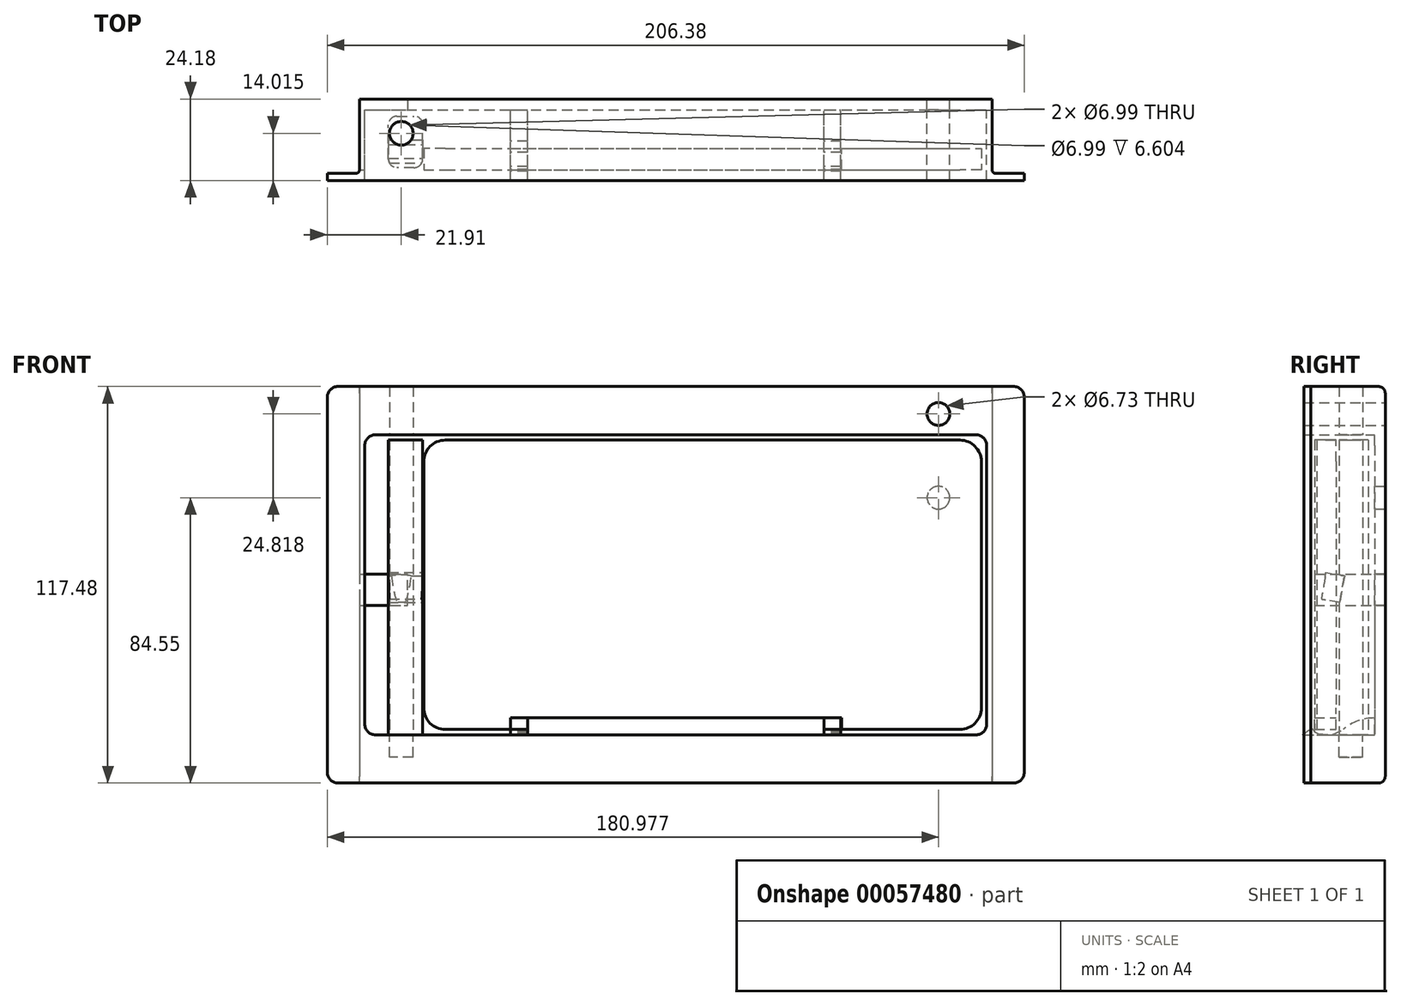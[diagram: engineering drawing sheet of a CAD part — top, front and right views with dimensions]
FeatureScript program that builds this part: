
annotation { "Feature Type Name" : "Feature", "Feature Type Description" : "" }
export const myFeature = defineFeature(function(context is Context, id is Id, definition is map)
    precondition{}
    {
        {
            var Q0;
            Q0=qCreatedBy(makeId("Front.planeOp"),FACE);
            var sketch = newSketch(context, id + "F0", { "sketchPlane" : qUnion([Q0])});
            skLineSegment(sketch, "E0.rect.bottom", {"start": v(-100.01, 58.74) * mm, "end": v(100.01, 58.74) * mm});
            skLineSegment(sketch, "E0.rect.top", {"start": v(-100.01, -58.74) * mm, "end": v(100.01, -58.74) * mm});
            skLineSegment(sketch, "E0.rect.left", {"start": v(-103.19, 55.56) * mm, "end": v(-103.19, -55.56) * mm});
            skLineSegment(sketch, "E0.rect.right", {"start": v(103.19, 55.56) * mm, "end": v(103.19, -55.56) * mm});
            skPoint(sketch, "E0.rect.middle", {"position": v(0, 0) * mm});
            skPoint(sketch, "E1.visualSharp", {"position": v(-103.19, 58.74) * mm});
            skArc(sketch, "E1.filletArc", {"start": v(-100.01, 58.74) * mm, "mid": v(-102.26, 57.8) * mm, "end": v(-103.19, 55.56) * mm});
            skPoint(sketch, "E2.visualSharp", {"position": v(103.19, 58.74) * mm});
            skArc(sketch, "E2.filletArc", {"start": v(103.19, 55.56) * mm, "mid": v(102.26, 57.8) * mm, "end": v(100.01, 58.74) * mm});
            skPoint(sketch, "E3.visualSharp", {"position": v(103.19, -58.74) * mm});
            skArc(sketch, "E3.filletArc", {"start": v(100.01, -58.74) * mm, "mid": v(102.26, -57.8) * mm, "end": v(103.19, -55.56) * mm});
            skPoint(sketch, "E4.visualSharp", {"position": v(-103.19, -58.74) * mm});
            skArc(sketch, "E4.filletArc", {"start": v(-103.19, -55.56) * mm, "mid": v(-102.26, -57.8) * mm, "end": v(-100.01, -58.74) * mm});
            skLineSegment(sketch, "E5.1", {"start": v(-92.07, 41.27) * mm, "end": v(-92.07, -41.28) * mm});
            skLineSegment(sketch, "E5.5", {"start": v(92.08, 41.28) * mm, "end": v(92.08, -41.27) * mm});
            skLineSegment(sketch, "E6", {"start": v(-88.9, 44.45) * mm, "end": v(88.9, 44.45) * mm});
            skLineSegment(sketch, "E7", {"start": v(-88.9, -44.45) * mm, "end": v(88.9, -44.45) * mm});
            skArc(sketch, "E8.filletArc", {"start": v(92.08, 41.28) * mm, "mid": v(91.15, 43.52) * mm, "end": v(88.9, 44.45) * mm});
            skArc(sketch, "E9.filletArc", {"start": v(88.9, -44.45) * mm, "mid": v(91.15, -43.52) * mm, "end": v(92.08, -41.27) * mm});
            skArc(sketch, "E10.filletArc", {"start": v(-92.07, -41.28) * mm, "mid": v(-91.15, -43.52) * mm, "end": v(-88.9, -44.45) * mm});
            skArc(sketch, "E11.filletArc", {"start": v(-88.9, 44.45) * mm, "mid": v(-91.15, 43.52) * mm, "end": v(-92.07, 41.27) * mm});
            skLineSegment(sketch, "E12", {"start": v(-103.19, 3.17) * mm, "end": v(-92.07, 3.17) * mm});
            skLineSegment(sketch, "E13", {"start": v(-103.19, -3.18) * mm, "end": v(-92.07, -3.18) * mm});
            skPoint(sketch, "E14.end.orphan", {"position": v(-103.19, 0) * mm});
            skPoint(sketch, "E14.start.orphan", {"position": v(-92.07, 0) * mm});
            skLineSegment(sketch, "E15", {"start": v(-92.07, 3.17) * mm, "end": v(-79.37, 3.17) * mm});
            skLineSegment(sketch, "E16", {"start": v(-92.07, -3.18) * mm, "end": v(-79.37, -3.18) * mm});
            skLineSegment(sketch, "E17", {"start": v(-79.37, -3.18) * mm, "end": v(-79.37, 3.17) * mm});
            skSolve(sketch);
        }
        {
            var Q0;
            Q0=makeQuery(id+"F0.imprint","IMPRINT",FACE,{"disambiguationData":[TD([[makeQuery(id+"F0.imprint","IMPRINT",EDGE,{"derivedFrom":sQuery(id+"F0.wireOp",EDGE,"E0.rect.bottom")}),-1.0]])]});
            var Q1;
            Q1=makeQuery(id+"F0.imprint","IMPRINT",FACE,{"disambiguationData":[TD([[makeQuery(id+"F0.imprint","IMPRINT",EDGE,{"derivedFrom":sQuery(id+"F0.wireOp",EDGE,"E5.5")}),-1.0]])]});
            extrude(context, id + "F1", {"entities" : qUnion([Q0, Q1]), "oppositeDirection" : true, "depth" : 3.17 * mm});
        }
        {
            var Q0;
            Q0=makeQuery(id+"F0.imprint","IMPRINT",FACE,{"disambiguationData":[TD([[makeQuery(id+"F0.imprint","IMPRINT",EDGE,{"derivedFrom":sQuery(id+"F0.wireOp",EDGE,"E0.rect.bottom")}),-1.0]])]});
            extrude(context, id + "F2", {"entities" : qUnion([Q0]), "operationType" : NewBodyOperationType.ADD, "depth" : 17.78 * mm});
        }
        {
            var Q0;
            Q0=makeQuery(id+"F2.opExtrude","CAP_FACE",FACE,{"disambiguationData":[OSD([sQuery(id+"F0.wireOp",EDGE,"E0.rect.bottom"),sQuery(id+"F0.wireOp",EDGE,"E0.rect.top"),sQuery(id+"F0.wireOp",EDGE,"E0.rect.left"),sQuery(id+"F0.wireOp",EDGE,"E0.rect.right"),sQuery(id+"F0.wireOp",EDGE,"E1.filletArc"),sQuery(id+"F0.wireOp",EDGE,"E2.filletArc"),sQuery(id+"F0.wireOp",EDGE,"E3.filletArc"),sQuery(id+"F0.wireOp",EDGE,"E4.filletArc"),sQuery(id+"F0.wireOp",EDGE,"E5.1"),sQuery(id+"F0.wireOp",EDGE,"E5.5"),sQuery(id+"F0.wireOp",EDGE,"E6"),sQuery(id+"F0.wireOp",EDGE,"E7"),sQuery(id+"F0.wireOp",EDGE,"E8.filletArc"),sQuery(id+"F0.wireOp",EDGE,"E9.filletArc"),sQuery(id+"F0.wireOp",EDGE,"E10.filletArc"),sQuery(id+"F0.wireOp",EDGE,"E11.filletArc"),sQuery(id+"F0.wireOp",EDGE,"E12"),sQuery(id+"F0.wireOp",EDGE,"E13")])],"isStart":false});
            var sketch = newSketch(context, id + "F3", { "sketchPlane" : qUnion([Q0])});
            skLineSegment(sketch, "E18", {"start": v(-88.9, 44.45) * mm, "end": v(88.9, 44.45) * mm});
            skLineSegment(sketch, "E19", {"start": v(92.08, 41.28) * mm, "end": v(92.08, -41.27) * mm});
            skLineSegment(sketch, "E20", {"start": v(88.9, -44.45) * mm, "end": v(-88.9, -44.45) * mm});
            skLineSegment(sketch, "E21", {"start": v(-92.07, -41.27) * mm, "end": v(-92.07, 41.27) * mm});
            skPoint(sketch, "E22.start.orphan", {"position": v(-91.15, 43.52) * mm});
            skLineSegment(sketch, "E23", {"start": v(-100.01, 58.74) * mm, "end": v(-100.01, 58.74) * mm});
            skLineSegment(sketch, "E24", {"start": v(-103.19, 55.56) * mm, "end": v(-103.19, -55.56) * mm});
            skLineSegment(sketch, "E25", {"start": v(-100.01, -58.74) * mm, "end": v(100.01, -58.74) * mm});
            skLineSegment(sketch, "E26", {"start": v(103.19, -55.56) * mm, "end": v(103.19, 55.56) * mm});
            skLineSegment(sketch, "E27", {"start": v(100.01, 58.74) * mm, "end": v(-100.01, 58.74) * mm});
            skPoint(sketch, "E28.visualSharp", {"position": v(-103.19, 58.74) * mm});
            skArc(sketch, "E28.filletArc", {"start": v(-100.01, 58.74) * mm, "mid": v(-102.26, 57.8) * mm, "end": v(-103.19, 55.56) * mm});
            skPoint(sketch, "E29.visualSharp", {"position": v(-92.07, 44.45) * mm});
            skArc(sketch, "E29.filletArc", {"start": v(-88.9, 44.45) * mm, "mid": v(-91.15, 43.52) * mm, "end": v(-92.07, 41.27) * mm});
            skPoint(sketch, "E30.visualSharp", {"position": v(92.08, 44.45) * mm});
            skArc(sketch, "E30.filletArc", {"start": v(92.08, 41.28) * mm, "mid": v(91.15, 43.52) * mm, "end": v(88.9, 44.45) * mm});
            skPoint(sketch, "E31.visualSharp", {"position": v(103.19, 58.74) * mm});
            skArc(sketch, "E31.filletArc", {"start": v(103.19, 55.56) * mm, "mid": v(102.26, 57.8) * mm, "end": v(100.01, 58.74) * mm});
            skPoint(sketch, "E32.visualSharp", {"position": v(92.08, -44.45) * mm});
            skArc(sketch, "E32.filletArc", {"start": v(88.9, -44.45) * mm, "mid": v(91.15, -43.52) * mm, "end": v(92.08, -41.27) * mm});
            skPoint(sketch, "E33.visualSharp", {"position": v(103.19, -58.74) * mm});
            skArc(sketch, "E33.filletArc", {"start": v(100.01, -58.74) * mm, "mid": v(102.26, -57.8) * mm, "end": v(103.19, -55.56) * mm});
            skPoint(sketch, "E34.visualSharp", {"position": v(-103.19, -58.74) * mm});
            skArc(sketch, "E34.filletArc", {"start": v(-103.19, -55.56) * mm, "mid": v(-102.26, -57.8) * mm, "end": v(-100.01, -58.74) * mm});
            skPoint(sketch, "E35.visualSharp", {"position": v(-92.07, -44.45) * mm});
            skArc(sketch, "E35.filletArc", {"start": v(-92.07, -41.27) * mm, "mid": v(-91.15, -43.52) * mm, "end": v(-88.9, -44.45) * mm});
            skSolve(sketch);
        }
        {
            var Q0;
            Q0=makeQuery(id+"F3.imprint","IMPRINT",FACE,{"disambiguationData":[TD([[makeQuery(id+"F3.imprint","IMPRINT",EDGE,{"derivedFrom":sQuery(id+"F3.wireOp",EDGE,"E18")}),1.0]])]});
            var Q1;
            {var subQ1=makeQuery(id+"F2.opExtrude","CAP_EDGE",EDGE,{"disambiguationData":[OSD([sQuery(id+"F0.wireOp",EDGE,"E12")])],"isStart":false});Q1=makeQuery(id+"F3.imprint","IMPRINT",FACE,{"disambiguationData":[TD([[makeQuery(id+"F3.imprint","IMPRINT",EDGE,{"derivedFrom":subQ1}),-1.0]])]});}
            extrude(context, id + "F4", {"entities" : qUnion([Q0, Q1]), "operationType" : NewBodyOperationType.ADD, "depth" : 3.17 * mm});
        }
        {
            var Q0;
            Q0=makeQuery(id+"F4.opExtrude","CAP_FACE",FACE,{"disambiguationData":[OSD([sQuery(id+"F3.wireOp",EDGE,"E18"),sQuery(id+"F3.wireOp",EDGE,"E19"),sQuery(id+"F3.wireOp",EDGE,"E20"),sQuery(id+"F3.wireOp",EDGE,"E21"),sQuery(id+"F3.wireOp",EDGE,"E24"),sQuery(id+"F3.wireOp",EDGE,"E25"),sQuery(id+"F3.wireOp",EDGE,"E26"),sQuery(id+"F3.wireOp",EDGE,"E27"),sQuery(id+"F3.wireOp",EDGE,"E28.filletArc"),sQuery(id+"F3.wireOp",EDGE,"E29.filletArc"),sQuery(id+"F3.wireOp",EDGE,"E30.filletArc"),sQuery(id+"F3.wireOp",EDGE,"E31.filletArc"),sQuery(id+"F3.wireOp",EDGE,"E32.filletArc"),sQuery(id+"F3.wireOp",EDGE,"E33.filletArc"),sQuery(id+"F3.wireOp",EDGE,"E34.filletArc"),sQuery(id+"F3.wireOp",EDGE,"E35.filletArc")])],"isStart":true});
            var sketch = newSketch(context, id + "F5", { "sketchPlane" : qUnion([Q0])});
            skLineSegment(sketch, "E36.rect.bottom", {"start": v(68.26, 42.86) * mm, "end": v(-84.14, 42.86) * mm});
            skLineSegment(sketch, "E36.rect.top", {"start": v(68.26, -42.86) * mm, "end": v(-84.14, -42.86) * mm});
            skLineSegment(sketch, "E36.rect.left", {"start": v(74.61, 36.51) * mm, "end": v(74.61, -36.51) * mm});
            skLineSegment(sketch, "E36.rect.right", {"start": v(-90.49, 36.51) * mm, "end": v(-90.49, -36.51) * mm});
            skPoint(sketch, "E36.rect.middle", {"position": v(-7.94, 0) * mm});
            skPoint(sketch, "E37.visualSharp", {"position": v(74.61, 42.86) * mm});
            skArc(sketch, "E37.filletArc", {"start": v(74.61, 36.51) * mm, "mid": v(72.75, 41) * mm, "end": v(68.26, 42.86) * mm});
            skPoint(sketch, "E38.visualSharp", {"position": v(-90.49, 42.86) * mm});
            skArc(sketch, "E38.filletArc", {"start": v(-84.14, 42.86) * mm, "mid": v(-88.63, 41) * mm, "end": v(-90.49, 36.51) * mm});
            skPoint(sketch, "E39.visualSharp", {"position": v(-90.49, -42.86) * mm});
            skArc(sketch, "E39.filletArc", {"start": v(-90.49, -36.51) * mm, "mid": v(-88.63, -41) * mm, "end": v(-84.14, -42.86) * mm});
            skPoint(sketch, "E40.visualSharp", {"position": v(74.61, -42.86) * mm});
            skArc(sketch, "E40.filletArc", {"start": v(68.26, -42.86) * mm, "mid": v(72.75, -41) * mm, "end": v(74.61, -36.51) * mm});
            skSolve(sketch);
        }
        {
            var Q0;
            Q0=makeQuery(id+"F5.imprint","IMPRINT",FACE,{"disambiguationData":[TD([[makeQuery(id+"F5.imprint","IMPRINT",EDGE,{"derivedFrom":sQuery(id+"F5.wireOp",EDGE,"E36.rect.bottom")}),1.0]])]});
            extrude(context, id + "F6", {"entities" : qUnion([Q0]), "operationType" : NewBodyOperationType.ADD, "depth" : 6.35 * mm});
        }
        {
            var Q0;
            Q0=makeQuery(id+"F4.boolean.opBoolean","MERGE",FACE,{"derivedFrom":[makeQuery(id+"F2.opExtrude","SWEPT_FACE",FACE,{"disambiguationData":[OSD([sQuery(id+"F0.wireOp",EDGE,"E6")])]}),makeQuery(id+"F4.opExtrude","SWEPT_FACE",FACE,{"disambiguationData":[OSD([sQuery(id+"F3.wireOp",EDGE,"E18")])]})]});
            var sketch = newSketch(context, id + "F7", { "sketchPlane" : qUnion([Q0])});
            skCircle(sketch, "E41", {"center": v(-81.28, 6.98) * mm, "radius": 3.5 * mm});
            skSolve(sketch);
        }
        {
            var Q0;
            Q0=makeQuery(id+"F7.imprint","IMPRINT",FACE,{"disambiguationData":[TD([[makeQuery(id+"F7.imprint","IMPRINT",EDGE,{"derivedFrom":sQuery(id+"F7.wireOp",EDGE,"E41")}),1.0]])]});
            extrude(context, id + "F8", {"entities" : qUnion([Q0]), "operationType" : NewBodyOperationType.REMOVE, "endBound" : BoundingType.UP_TO_NEXT, "oppositeDirection" : true, "depth" : 6.35 * mm});
        }
        {
            var Q0;
            Q0=makeQuery(id+"F4.boolean.opBoolean","MERGE",FACE,{"derivedFrom":[makeQuery(id+"F2.opExtrude","SWEPT_FACE",FACE,{"disambiguationData":[OSD([sQuery(id+"F0.wireOp",EDGE,"E7")])]}),makeQuery(id+"F4.opExtrude","SWEPT_FACE",FACE,{"disambiguationData":[OSD([sQuery(id+"F3.wireOp",EDGE,"E20")])]})]});
            var sketch = newSketch(context, id + "F9", { "sketchPlane" : qUnion([Q0])});
            skCircle(sketch, "E42", {"center": v(-81.28, -6.98) * mm, "radius": 3.5 * mm});
            skSolve(sketch);
        }
        {
            var Q0;
            Q0=makeQuery(id+"F9.imprint","IMPRINT",FACE,{"disambiguationData":[TD([[makeQuery(id+"F9.imprint","IMPRINT",EDGE,{"derivedFrom":sQuery(id+"F9.wireOp",EDGE,"E42")}),1.0]])]});
            extrude(context, id + "F10", {"entities" : qUnion([Q0]), "operationType" : NewBodyOperationType.REMOVE, "oppositeDirection" : true, "depth" : 6.6 * mm});
        }
        {
            var Q0;
            Q0=makeQuery(id+"F4.boolean.opBoolean","MERGE",FACE,{"derivedFrom":[makeQuery(id+"F2.opExtrude","SWEPT_FACE",FACE,{"disambiguationData":[OSD([sQuery(id+"F0.wireOp",EDGE,"E7")])]}),makeQuery(id+"F4.opExtrude","SWEPT_FACE",FACE,{"disambiguationData":[OSD([sQuery(id+"F3.wireOp",EDGE,"E20")])]})]});
            var sketch = newSketch(context, id + "F11", { "sketchPlane" : qUnion([Q0])});
            skCircle(sketch, "E43", {"center": v(-81.28, -6.98) * mm, "radius": 3.3 * mm});
            skLineSegment(sketch, "E44", {"start": v(-74.93, -17.14) * mm, "end": v(-85.1, -17.14) * mm});
            skLineSegment(sketch, "E45", {"start": v(-85.1, -17.14) * mm, "end": v(-85.1, -1.9) * mm});
            skLineSegment(sketch, "E46", {"start": v(-85.1, -1.9) * mm, "end": v(-74.93, -1.9) * mm});
            skLineSegment(sketch, "E47", {"start": v(-74.93, -17.14) * mm, "end": v(-74.93, -1.9) * mm});
            skSolve(sketch);
        }
        {
            var Q0;
            Q0=makeQuery(id+"F11.imprint","IMPRINT",FACE,{"disambiguationData":[TD([[makeQuery(id+"F11.imprint","IMPRINT",EDGE,{"derivedFrom":sQuery(id+"F11.wireOp",EDGE,"E44")}),-1.0]])]});
            var Q1;
            Q1 = qSketchRegion(id + "F13", true);
            extrude(context, id + "F12", {"entities" : qUnion([Q0, Q1]), "depth" : 87.31 * mm});
        }
        {
            var Q0;
            Q0=makeQuery(id+"F12.opExtrude","SWEPT_FACE",FACE,{"disambiguationData":[OSD([sQuery(id+"F11.wireOp",EDGE,"E47")])]});
            var sketch = newSketch(context, id + "F13", { "sketchPlane" : qUnion([Q0])});
            skPoint(sketch, "E48.rect.middle", {"position": v(-10.27, -5.18) * mm});
            skLineSegment(sketch, "E49", {"start": v(-10.27, -5.18) * mm, "end": v(-15.74, -4.21) * mm});
            skLineSegment(sketch, "E50", {"start": v(-15.74, -4.21) * mm, "end": v(-14.37, 3.6) * mm});
            skLineSegment(sketch, "E51", {"start": v(-14.37, 3.6) * mm, "end": v(-8.9, 2.64) * mm});
            skLineSegment(sketch, "E52", {"start": v(-8.9, 2.64) * mm, "end": v(-10.27, -5.18) * mm});
            skPoint(sketch, "E53.end.orphan", {"position": v(-15.05, -0.3) * mm});
            skPoint(sketch, "E53.start.orphan", {"position": v(-12.32, -0.79) * mm});
            skSolve(sketch);
        }
        {
            var Q0;
            Q0=makeQuery(id+"F13.imprint","IMPRINT",FACE,{"disambiguationData":[TD([[makeQuery(id+"F13.imprint","IMPRINT",EDGE,{"derivedFrom":sQuery(id+"F13.wireOp",EDGE,"E49")}),-1.0]])]});
            extrude(context, id + "F14", {"entities" : qUnion([Q0]), "operationType" : NewBodyOperationType.REMOVE, "endBound" : BoundingType.UP_TO_NEXT, "oppositeDirection" : true, "depth" : 25.4 * mm});
        }
        {
            var Q0;
            Q0=makeQuery(id+"F12.opExtrude","SWEPT_EDGE",EDGE,{"disambiguationData":[OSD([sQuery(id+"F11.wireOp",EDGE,"E44"),sQuery(id+"F11.wireOp",EDGE,"E45")])]});
            var Q1;
            Q1=makeQuery(id+"F12.opExtrude","SWEPT_EDGE",EDGE,{"disambiguationData":[OSD([sQuery(id+"F11.wireOp",EDGE,"E44"),sQuery(id+"F11.wireOp",EDGE,"E47")])]});
            var Q2;
            Q2=makeQuery(id+"F12.opExtrude","SWEPT_EDGE",EDGE,{"disambiguationData":[OSD([sQuery(id+"F11.wireOp",EDGE,"E46"),sQuery(id+"F11.wireOp",EDGE,"E47")])]});
            var Q3;
            Q3=makeQuery(id+"F12.opExtrude","SWEPT_EDGE",EDGE,{"disambiguationData":[OSD([sQuery(id+"F11.wireOp",EDGE,"E45"),sQuery(id+"F11.wireOp",EDGE,"E46")])]});
            fillet(context, id + "F15", {"entities" : qUnion([Q0, Q1, Q2, Q3]), "radius" : 2.54 * mm, "tangentPropagation" : true, "allowEdgeOverflow" : false});
        }
        {
            var Q0;
            Q0=makeQuery(id+"F1.opExtrude","CAP_FACE",FACE,{"disambiguationData":[OSD([sQuery(id+"F0.wireOp",EDGE,"E0.rect.bottom"),sQuery(id+"F0.wireOp",EDGE,"E0.rect.top"),sQuery(id+"F0.wireOp",EDGE,"E0.rect.left"),sQuery(id+"F0.wireOp",EDGE,"E0.rect.right"),sQuery(id+"F0.wireOp",EDGE,"E1.filletArc"),sQuery(id+"F0.wireOp",EDGE,"E2.filletArc"),sQuery(id+"F0.wireOp",EDGE,"E3.filletArc"),sQuery(id+"F0.wireOp",EDGE,"E4.filletArc"),sQuery(id+"F0.wireOp",EDGE,"E12"),sQuery(id+"F0.wireOp",EDGE,"E13"),sQuery(id+"F0.wireOp",EDGE,"E15"),sQuery(id+"F0.wireOp",EDGE,"E16"),sQuery(id+"F0.wireOp",EDGE,"E17")])],"isStart":false});
            var sketch = newSketch(context, id + "F16", { "sketchPlane" : qUnion([Q0])});
            skCircle(sketch, "E54", {"center": v(-77.79, 50.63) * mm, "radius": 3.37 * mm});
            skCircle(sketch, "E55", {"center": v(-77.79, 25.81) * mm, "radius": 3.37 * mm});
            skSolve(sketch);
        }
        {
            var Q0;
            Q0=makeQuery(id+"F16.imprint","IMPRINT",FACE,{"disambiguationData":[TD([[makeQuery(id+"F16.imprint","IMPRINT",EDGE,{"derivedFrom":sQuery(id+"F16.wireOp",EDGE,"E54")}),1.0]])]});
            extrude(context, id + "F17", {"entities" : qUnion([Q0]), "operationType" : NewBodyOperationType.REMOVE, "oppositeDirection" : true, "depth" : 24.6 * mm});
        }
        {
            var Q0;
            Q0=makeQuery(id+"F16.imprint","IMPRINT",FACE,{"disambiguationData":[TD([[makeQuery(id+"F16.imprint","IMPRINT",EDGE,{"derivedFrom":sQuery(id+"F16.wireOp",EDGE,"E55")}),1.0]])]});
            extrude(context, id + "F18", {"entities" : qUnion([Q0]), "operationType" : NewBodyOperationType.REMOVE, "endBound" : BoundingType.UP_TO_NEXT, "oppositeDirection" : true, "depth" : 25.4 * mm});
        }
        {
            var Q0;
            Q0=makeQuery(id+"F16.imprint","IMPRINT",FACE,{"disambiguationData":[TD([[makeQuery(id+"F16.imprint","IMPRINT",EDGE,{"derivedFrom":sQuery(id+"F16.wireOp",EDGE,"E54")}),-1.0]])]});
            var sketch = newSketch(context, id + "F19", { "sketchPlane" : qUnion([Q0])});
            skLineSegment(sketch, "E56", {"start": v(-93.66, 58.74) * mm, "end": v(-93.66, -58.74) * mm});
            skLineSegment(sketch, "E57", {"start": v(93.66, 58.74) * mm, "end": v(93.66, -58.74) * mm});
            skLineSegment(sketch, "E58", {"start": v(93.66, 58.74) * mm, "end": v(103.19, 58.74) * mm});
            skLineSegment(sketch, "E59.bottom", {"start": v(103.19, 58.74) * mm, "end": v(93.66, 58.74) * mm});
            skLineSegment(sketch, "E59.top", {"start": v(103.19, -58.74) * mm, "end": v(93.66, -58.74) * mm});
            skLineSegment(sketch, "E59.left", {"start": v(103.19, 58.74) * mm, "end": v(103.19, -58.74) * mm});
            skLineSegment(sketch, "E60.bottom", {"start": v(-93.66, 58.74) * mm, "end": v(-103.19, 58.74) * mm});
            skLineSegment(sketch, "E60.top", {"start": v(-93.66, -58.74) * mm, "end": v(-103.19, -58.74) * mm});
            skLineSegment(sketch, "E60.right", {"start": v(-103.19, 58.74) * mm, "end": v(-103.19, -58.74) * mm});
            skSolve(sketch);
        }
        {
            var Q0;
            {var subQ3=sQuery(id+"F19.wireOp",EDGE,"E56");Q0=makeQuery(id+"F19.imprint","IMPRINT",FACE,{"disambiguationData":[TD([[makeQuery(id+"F19.imprint","IMPRINT",EDGE,{"derivedFrom":subQ3}),-1.0]])]});}
            var Q1;
            {var subQ5=makeQuery(id+"F16.imprint","IMPRINT",EDGE,{"derivedFrom":makeQuery(id+"F1.opExtrude","CAP_EDGE",EDGE,{"disambiguationData":[OSD([sQuery(id+"F0.wireOp",EDGE,"E1.filletArc")])],"isStart":false})});Q1=makeQuery(id+"F19.imprint","IMPRINT",FACE,{"disambiguationData":[TD([[makeQuery(id+"F19.imprint","IMPRINT",EDGE,{"derivedFrom":subQ5}),-1.0]])]});}
            var Q2;
            {var subQ0=makeQuery(id+"F16.imprint","IMPRINT",EDGE,{"derivedFrom":makeQuery(id+"F1.opExtrude","CAP_EDGE",EDGE,{"disambiguationData":[OSD([sQuery(id+"F0.wireOp",EDGE,"E4.filletArc")])],"isStart":false})});Q2=makeQuery(id+"F19.imprint","IMPRINT",FACE,{"disambiguationData":[TD([[makeQuery(id+"F19.imprint","IMPRINT",EDGE,{"derivedFrom":subQ0}),-1.0]])]});}
            extrude(context, id + "F20", {"entities" : qUnion([Q0, Q1, Q2]), "operationType" : NewBodyOperationType.REMOVE, "oppositeDirection" : true, "depth" : 22 * mm});
        }
        {
            var Q0;
            Q0=makeQuery(id+"F4.opExtrude","CAP_FACE",FACE,{"disambiguationData":[OSD([sQuery(id+"F3.wireOp",EDGE,"E18"),sQuery(id+"F3.wireOp",EDGE,"E19"),sQuery(id+"F3.wireOp",EDGE,"E20"),sQuery(id+"F3.wireOp",EDGE,"E21"),sQuery(id+"F3.wireOp",EDGE,"E24"),sQuery(id+"F3.wireOp",EDGE,"E25"),sQuery(id+"F3.wireOp",EDGE,"E26"),sQuery(id+"F3.wireOp",EDGE,"E27"),sQuery(id+"F3.wireOp",EDGE,"E28.filletArc"),sQuery(id+"F3.wireOp",EDGE,"E29.filletArc"),sQuery(id+"F3.wireOp",EDGE,"E30.filletArc"),sQuery(id+"F3.wireOp",EDGE,"E31.filletArc"),sQuery(id+"F3.wireOp",EDGE,"E32.filletArc"),sQuery(id+"F3.wireOp",EDGE,"E33.filletArc"),sQuery(id+"F3.wireOp",EDGE,"E34.filletArc"),sQuery(id+"F3.wireOp",EDGE,"E35.filletArc")])],"isStart":true});
            var sketch = newSketch(context, id + "F21", { "sketchPlane" : qUnion([Q0])});
            skLineSegment(sketch, "E61.bottom", {"start": v(93.66, 3.17) * mm, "end": v(103.19, 3.17) * mm});
            skLineSegment(sketch, "E61.top", {"start": v(93.66, -3.18) * mm, "end": v(103.19, -3.18) * mm});
            skLineSegment(sketch, "E61.left", {"start": v(93.66, 3.17) * mm, "end": v(93.66, -3.18) * mm});
            skLineSegment(sketch, "E61.right", {"start": v(103.19, 3.17) * mm, "end": v(103.19, -3.18) * mm});
            skSolve(sketch);
        }
        {
            var Q0;
            Q0=makeQuery(id+"F21.imprint","IMPRINT",FACE,{"disambiguationData":[TD([[makeQuery(id+"F21.imprint","IMPRINT",EDGE,{"derivedFrom":sQuery(id+"F21.wireOp",EDGE,"E61.bottom")}),1.0]])]});
            extrude(context, id + "F22", {"entities" : qUnion([Q0]), "operationType" : NewBodyOperationType.REMOVE, "oppositeDirection" : true, "depth" : 1.05 * mm});
        }
        {
            var Q0;
            {var subQ0=sQuery(id+"F19.wireOp",EDGE,"E57");Q0=makeQuery(id+"F20.boolean.opBoolean","COPY",EDGE,{"derivedFrom":makeQuery(id+"F20.opExtrude","CAP_EDGE",EDGE,{"disambiguationData":[OSD([subQ0]),TDD([makeQuery(id+"F19.imprint","IMPRINT",EDGE,{"disambiguationData":[TD([[makeQuery(id+"F19.imprint","INTERSECT",VERTEX,{"derivedFrom":[makeQuery(id+"F16.imprint","IMPRINT",EDGE,{"derivedFrom":makeQuery(id+"F1.opExtrude","CAP_EDGE",EDGE,{"disambiguationData":[OSD([sQuery(id+"F0.wireOp",EDGE,"E0.rect.top")])],"isStart":false})}),sQuery(id+"F19.wireOp",EDGE,"E59.top"),subQ0]}),1.0]])],"derivedFrom":subQ0})])],"isStart":false})});}
            var Q1;
            {var subQ0=sQuery(id+"F19.wireOp",EDGE,"E57");Q1=makeQuery(id+"F20.boolean.opBoolean","COPY",EDGE,{"derivedFrom":makeQuery(id+"F20.opExtrude","CAP_EDGE",EDGE,{"disambiguationData":[OSD([subQ0]),TDD([makeQuery(id+"F19.imprint","IMPRINT",EDGE,{"disambiguationData":[TD([[makeQuery(id+"F19.imprint","INTERSECT",VERTEX,{"derivedFrom":[makeQuery(id+"F16.imprint","IMPRINT",EDGE,{"derivedFrom":makeQuery(id+"F1.opExtrude","CAP_EDGE",EDGE,{"disambiguationData":[OSD([sQuery(id+"F0.wireOp",EDGE,"E0.rect.bottom")])],"isStart":false})}),sQuery(id+"F19.wireOp",EDGE,"E59.bottom"),subQ0]}),-1.0]])],"derivedFrom":subQ0})])],"isStart":false})});}
            var Q2;
            Q2=makeQuery(id+"F20.boolean.opBoolean","COPY",EDGE,{"derivedFrom":makeQuery(id+"F20.opExtrude","CAP_EDGE",EDGE,{"disambiguationData":[OSD([sQuery(id+"F19.wireOp",EDGE,"E56")])],"isStart":false})});
            fillet(context, id + "F23", {"entities" : qUnion([Q0, Q1, Q2]), "radius" : 1 * mm, "tangentPropagation" : true, "allowEdgeOverflow" : false});
        }
        {
            var Q0;
            Q0=makeQuery(id+"F1.opExtrude","CAP_EDGE",EDGE,{"disambiguationData":[OSD([sQuery(id+"F0.wireOp",EDGE,"E0.rect.bottom")])],"isStart":false});
            var Q1;
            {var subQ0=sQuery(id+"F19.wireOp",EDGE,"E57");Q1=makeQuery(id+"F20.boolean.opBoolean","COPY",EDGE,{"derivedFrom":makeQuery(id+"F20.opExtrude","CAP_EDGE",EDGE,{"disambiguationData":[OSD([subQ0]),TDD([makeQuery(id+"F19.imprint","IMPRINT",EDGE,{"disambiguationData":[TD([[makeQuery(id+"F19.imprint","INTERSECT",VERTEX,{"derivedFrom":[makeQuery(id+"F16.imprint","IMPRINT",EDGE,{"derivedFrom":makeQuery(id+"F1.opExtrude","CAP_EDGE",EDGE,{"disambiguationData":[OSD([sQuery(id+"F0.wireOp",EDGE,"E0.rect.bottom")])],"isStart":false})}),sQuery(id+"F19.wireOp",EDGE,"E59.bottom"),subQ0]}),-1.0]])],"derivedFrom":subQ0})])],"isStart":true})});}
            var Q2;
            {var subQ0=sQuery(id+"F19.wireOp",EDGE,"E57");Q2=makeQuery(id+"F20.boolean.opBoolean","COPY",EDGE,{"derivedFrom":makeQuery(id+"F20.opExtrude","CAP_EDGE",EDGE,{"disambiguationData":[OSD([subQ0]),TDD([makeQuery(id+"F19.imprint","IMPRINT",EDGE,{"disambiguationData":[TD([[makeQuery(id+"F19.imprint","INTERSECT",VERTEX,{"derivedFrom":[makeQuery(id+"F16.imprint","IMPRINT",EDGE,{"derivedFrom":makeQuery(id+"F1.opExtrude","CAP_EDGE",EDGE,{"disambiguationData":[OSD([sQuery(id+"F0.wireOp",EDGE,"E0.rect.top")])],"isStart":false})}),sQuery(id+"F19.wireOp",EDGE,"E59.top"),subQ0]}),1.0]])],"derivedFrom":subQ0})])],"isStart":true})});}
            var Q3;
            Q3=makeQuery(id+"F1.opExtrude","CAP_EDGE",EDGE,{"disambiguationData":[OSD([sQuery(id+"F0.wireOp",EDGE,"E0.rect.top")])],"isStart":false});
            var Q4;
            Q4=makeQuery(id+"F20.boolean.opBoolean","COPY",EDGE,{"derivedFrom":makeQuery(id+"F20.opExtrude","CAP_EDGE",EDGE,{"disambiguationData":[OSD([sQuery(id+"F19.wireOp",EDGE,"E56")])],"isStart":true})});
            var Q5;
            Q5=makeQuery(id+"F20.boolean.opBoolean","COPY",EDGE,{"derivedFrom":makeQuery(id+"F20.opExtrude","SWEPT_EDGE",EDGE,{"disambiguationData":[OSD([sQuery(id+"F0.wireOp",EDGE,"E0.rect.bottom"),sQuery(id+"F19.wireOp",EDGE,"E59.bottom"),sQuery(id+"F19.wireOp",EDGE,"E57")])]})});
            var Q6;
            Q6=makeQuery(id+"F20.boolean.opBoolean","COPY",EDGE,{"derivedFrom":makeQuery(id+"F20.opExtrude","SWEPT_EDGE",EDGE,{"disambiguationData":[OSD([sQuery(id+"F0.wireOp",EDGE,"E0.rect.bottom"),sQuery(id+"F19.wireOp",EDGE,"E60.bottom"),sQuery(id+"F19.wireOp",EDGE,"E56")])]})});
            fillet(context, id + "F24", {"entities" : qUnion([Q0, Q1, Q2, Q3, Q4, Q5, Q6]), "radius" : 2 * mm, "tangentPropagation" : true, "allowEdgeOverflow" : false});
        }
        {
            var Q0;
            Q0=makeQuery(id+"F1.opExtrude","CAP_FACE",FACE,{"disambiguationData":[OSD([sQuery(id+"F0.wireOp",EDGE,"E0.rect.bottom"),sQuery(id+"F0.wireOp",EDGE,"E0.rect.top"),sQuery(id+"F0.wireOp",EDGE,"E0.rect.left"),sQuery(id+"F0.wireOp",EDGE,"E0.rect.right"),sQuery(id+"F0.wireOp",EDGE,"E1.filletArc"),sQuery(id+"F0.wireOp",EDGE,"E2.filletArc"),sQuery(id+"F0.wireOp",EDGE,"E3.filletArc"),sQuery(id+"F0.wireOp",EDGE,"E4.filletArc"),sQuery(id+"F0.wireOp",EDGE,"E12"),sQuery(id+"F0.wireOp",EDGE,"E13"),sQuery(id+"F0.wireOp",EDGE,"E15"),sQuery(id+"F0.wireOp",EDGE,"E16"),sQuery(id+"F0.wireOp",EDGE,"E17")])],"isStart":true});
            var sketch = newSketch(context, id + "F25", { "sketchPlane" : qUnion([Q0])});
            skLineSegment(sketch, "E62.bottom", {"start": v(-48.9, -44.45) * mm, "end": v(-43.9, -44.45) * mm});
            skLineSegment(sketch, "E62.top", {"start": v(-48.9, -39.45) * mm, "end": v(-43.9, -39.45) * mm});
            skLineSegment(sketch, "E62.left", {"start": v(-48.9, -44.45) * mm, "end": v(-48.9, -39.45) * mm});
            skLineSegment(sketch, "E62.right", {"start": v(-43.9, -44.45) * mm, "end": v(-43.9, -39.45) * mm});
            skLineSegment(sketch, "E63.bottom", {"start": v(43.9, -44.45) * mm, "end": v(48.9, -44.45) * mm});
            skLineSegment(sketch, "E63.top", {"start": v(43.9, -39.45) * mm, "end": v(48.9, -39.45) * mm});
            skLineSegment(sketch, "E63.left", {"start": v(43.9, -44.45) * mm, "end": v(43.9, -39.45) * mm});
            skLineSegment(sketch, "E63.right", {"start": v(48.9, -44.45) * mm, "end": v(48.9, -39.45) * mm});
            skSolve(sketch);
        }
        {
            var Q0;
            Q0=makeQuery(id+"F25.imprint","IMPRINT",FACE,{"disambiguationData":[TD([[makeQuery(id+"F25.imprint","IMPRINT",EDGE,{"derivedFrom":sQuery(id+"F25.wireOp",EDGE,"E62.bottom")}),1.0]])]});
            var Q1;
            Q1=makeQuery(id+"F25.imprint","IMPRINT",FACE,{"disambiguationData":[TD([[makeQuery(id+"F25.imprint","IMPRINT",EDGE,{"derivedFrom":sQuery(id+"F25.wireOp",EDGE,"E63.bottom")}),1.0]])]});
            extrude(context, id + "F26", {"entities" : qUnion([Q0, Q1]), "depth" : 21 * mm});
        }
        {
            var Q0;
            Q0=makeQuery(id+"F26.opExtrude","SWEPT_FACE",FACE,{"disambiguationData":[OSD([sQuery(id+"F25.wireOp",EDGE,"E62.left")])]});
            var sketch = newSketch(context, id + "F27", { "sketchPlane" : qUnion([Q0])});
            skArc(sketch, "E64", {"start": v(21, -44.45) * mm, "mid": v(19.76, -43.36) * mm, "end": v(18.2, -42.86) * mm});
            skArc(sketch, "E65", {"start": v(9.27, -42.86) * mm, "mid": v(4.94, -40.33) * mm, "end": v(0, -39.45) * mm});
            skLineSegment(sketch, "E66", {"start": v(0, -39.45) * mm, "end": v(21, -39.45) * mm});
            skLineSegment(sketch, "E67", {"start": v(21, -39.45) * mm, "end": v(21, -44.45) * mm});
            skLineSegment(sketch, "E68", {"start": v(18.2, -42.86) * mm, "end": v(17.7, -43.53) * mm});
            skPoint(sketch, "E69.endSnap0", {"position": v(13.33, -43.62) * mm});
            skPoint(sketch, "E70.orphan", {"position": v(17.4, -42.86) * mm});
            skLineSegment(sketch, "E71", {"start": v(17.7, -43.53) * mm, "end": v(16.76, -44.13) * mm});
            skLineSegment(sketch, "E72", {"start": v(16.76, -44.13) * mm, "end": v(12.62, -44.45) * mm});
            skLineSegment(sketch, "E73", {"start": v(12.62, -44.45) * mm, "end": v(9.27, -42.86) * mm});
            skPoint(sketch, "E69.end.orphan", {"position": v(13.33, -43.63) * mm});
            skSolve(sketch);
        }
        {
            var Q0;
            Q0=makeQuery(id+"F27.imprint","IMPRINT",FACE,{"disambiguationData":[TD([[makeQuery(id+"F27.imprint","IMPRINT",EDGE,{"derivedFrom":sQuery(id+"F27.wireOp",EDGE,"E64")}),-1.0]])]});
            extrude(context, id + "F28", {"entities" : qUnion([Q0]), "operationType" : NewBodyOperationType.REMOVE, "oppositeDirection" : true, "depth" : 98 * mm});
        }
        {
            var Q0;
            {var subQ0=sQuery(id+"F0.wireOp",EDGE,"E13");Q0=makeQuery(id+"F2.boolean.opBoolean","MERGE",FACE,{"derivedFrom":[makeQuery(id+"F1.opExtrude","SWEPT_FACE",FACE,{"disambiguationData":[OSD([subQ0,sQuery(id+"F0.wireOp",EDGE,"E16")])]}),makeQuery(id+"F2.opExtrude","SWEPT_FACE",FACE,{"disambiguationData":[OSD([subQ0])]})]});}
            extrude(context, id + "F29", {"entities" : qUnion([Q0]), "operationType" : NewBodyOperationType.REMOVE, "oppositeDirection" : true, "depth" : 3 * mm});
        }
    });
